SOLIDWORKS PART (.sldprt)
format: sldprt  version: not decoded by parser v0  size: 804,352 bytes
history: native  units: mm
features: plane x5, revolve x4, sketch x3, pattern_linear x2, extrude x1 + 1 further entry (+6 scaffold rows collapsed)
feature tree (22):
  scaffold x6  (default folders/planes/origin — collapsed)
  "Corps de surface"
  plane  "Face"
  plane  "Dessus"
  plane  "Droite"
  sketch  "Esquisse1"  dims[D1=24.0mm D2=0.1mm D3=8.0mm D4=0.1mm]
  extrude  "Lien1"  Depth=400mm
  sketch  "cercle1"  dims[D1=20.0mm D2=12.0mm]
  sketch  "Esquisse3"  dims[c1.D1=0.4mm c1.D2=7.0mm c1.D3=2.0mm c1.D4=6.0mm c1.D5=~3.166456mm c2.D5=20.0deg c2.D6=2.9mm c2.D3=~0.72794mm]
  revolve  "Révolution1"  Angle=360deg
  revolve  "Axe2"  [1 undecoded]
  revolve  "Axe3"  [1 undecoded]
  pattern_linear  "Répétition linéaire1"  Count1=4 Count2=1 Spacing1=4mm Spacing2=50mm
  pattern_linear  "Répétition linéaire2"  Count1=21 Count2=2 Spacing1=20mm Spacing2=8.9mm
  plane  "Plan1"  Offset=10mm
  plane  "Plan2"  Offset=12mm
  revolve  "Axe4"  [1 undecoded]
decode coverage: 7 of 10 modeling features carry decoded parameters; 1 rows unclassified (native names shown)
note: ~ marks probable driven/reference dimensions
note: 3 parameter values undecoded
summary: no parameter record found for 3 features
note: suppression state not decoded; provenance and decode notes live in map.json
